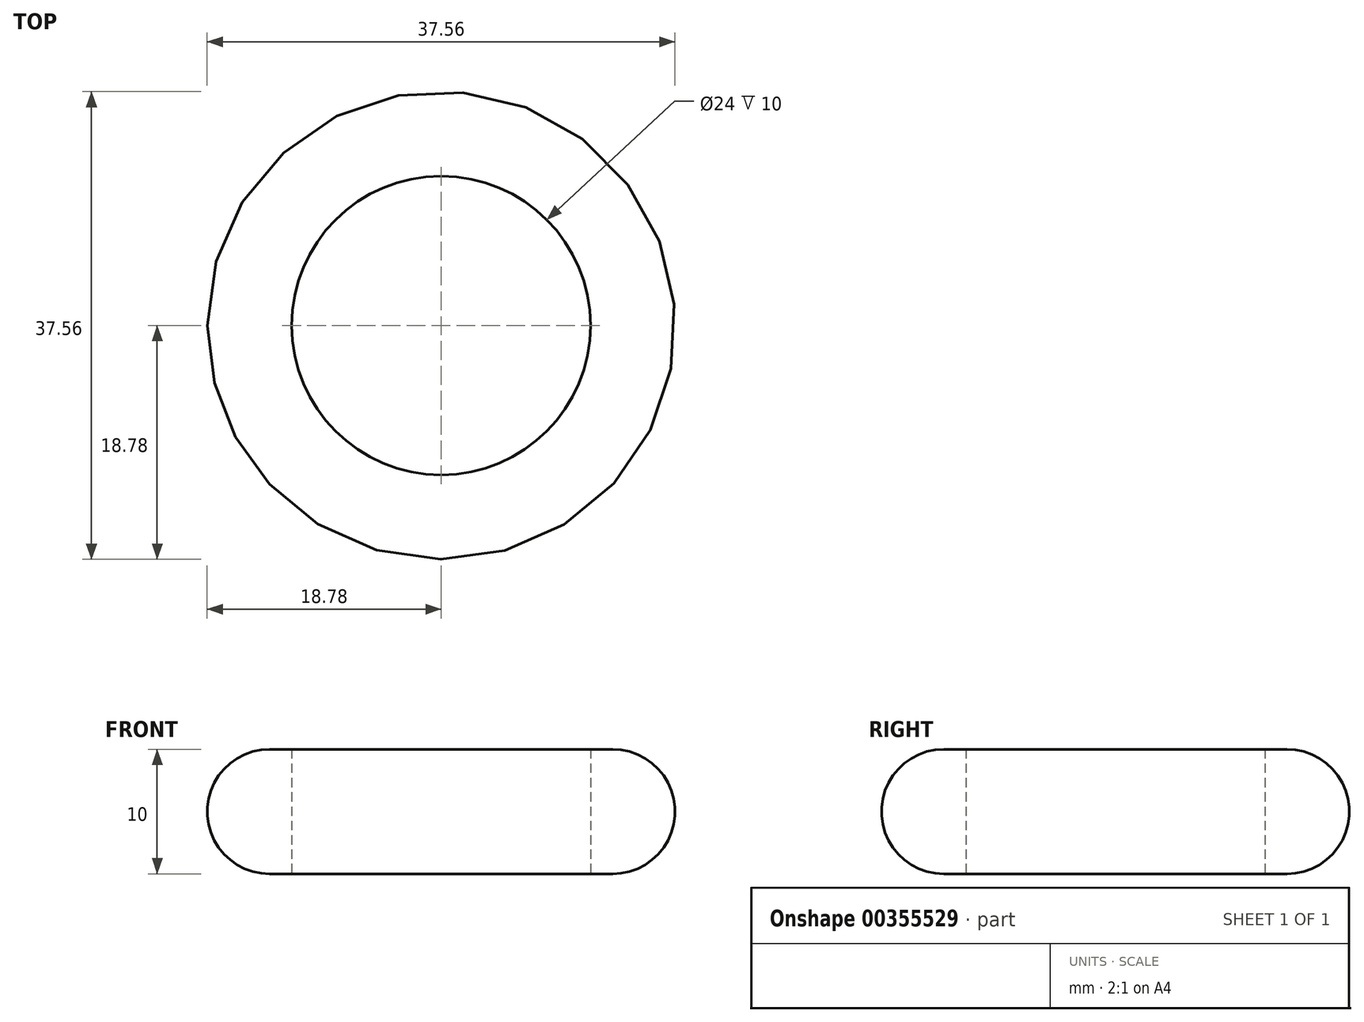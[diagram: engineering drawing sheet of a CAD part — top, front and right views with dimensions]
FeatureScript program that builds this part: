
annotation { "Feature Type Name" : "Feature", "Feature Type Description" : "" }
export const myFeature = defineFeature(function(context is Context, id is Id, definition is map)
    precondition{}
    {
        {
            var Q0;
            Q0=qCreatedBy(makeId("Front.planeOp"),FACE);
            var sketch = newSketch(context, id + "F0", { "sketchPlane" : qUnion([Q0])});
            skLineSegment(sketch, "E0.bottom", {"start": v(0, 0) * mm, "end": v(-1.78, 0) * mm});
            skLineSegment(sketch, "E0.top", {"start": v(0, 10) * mm, "end": v(-1.78, 10) * mm});
            skLineSegment(sketch, "E0.left", {"start": v(0, 0) * mm, "end": v(0, 10) * mm});
            skLineSegment(sketch, "E1", {"start": v(-6.78, 5) * mm, "end": v(-6.78, 5) * mm});
            skPoint(sketch, "E2.visualSharp", {"position": v(-4, 10) * mm});
            skArc(sketch, "E2.filletArc", {"start": v(-1.78, 10) * mm, "mid": v(-5.31, 8.54) * mm, "end": v(-6.78, 5) * mm});
            skPoint(sketch, "E3.visualSharp", {"position": v(-4, 0) * mm});
            skArc(sketch, "E3.filletArc", {"start": v(-6.78, 5) * mm, "mid": v(-5.31, 1.46) * mm, "end": v(-1.78, 0) * mm});
            skLineSegment(sketch, "E4.0", {"start": v(12, 0) * mm, "end": v(12, 10) * mm});
            skSolve(sketch);
        }
        {
            var Q0;
            Q0=makeQuery(id+"F0.imprint","IMPRINT",FACE,{"disambiguationData":[TD([[makeQuery(id+"F0.imprint","IMPRINT",EDGE,{"derivedFrom":sQuery(id+"F0.wireOp",EDGE,"E0.bottom")}),-1.0]])]});
            var Q1;
            Q1=sQuery(id+"F0.wireOp",EDGE,"E4.0");
            revolve(context, id + "F1", {"entities" : qUnion([Q0]), "axis" : qUnion([Q1]), "revolveType" : RevolveType.FULL});
        }
    });
